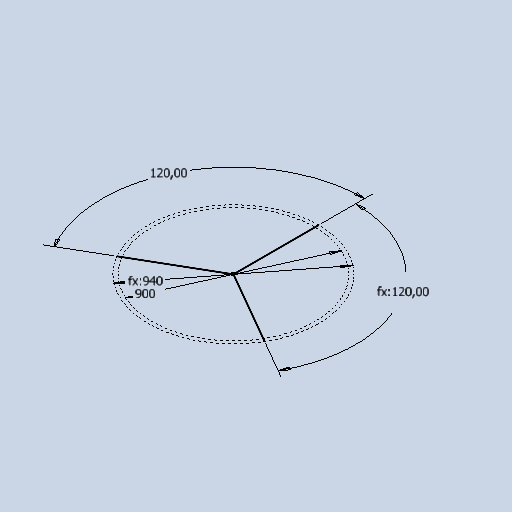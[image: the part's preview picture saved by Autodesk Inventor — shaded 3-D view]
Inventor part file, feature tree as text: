
AUTODESK INVENTOR PART (.ipt)
format: ipt  version: 2025.1 (Build 291241020, 241B)  size: 132,608 bytes
history: native  units: mm
features: sketch x1
ambient origin geometry x8: Origin, YZ Plane, XZ Plane, XY Plane, X Axis, Y Axis, Z Axis, Center Point
feature tree (1):
  sketch  "Sketch1"  dims[d1=900.0mm d2=120.0deg d3=120.0deg d4=940.0mm]
